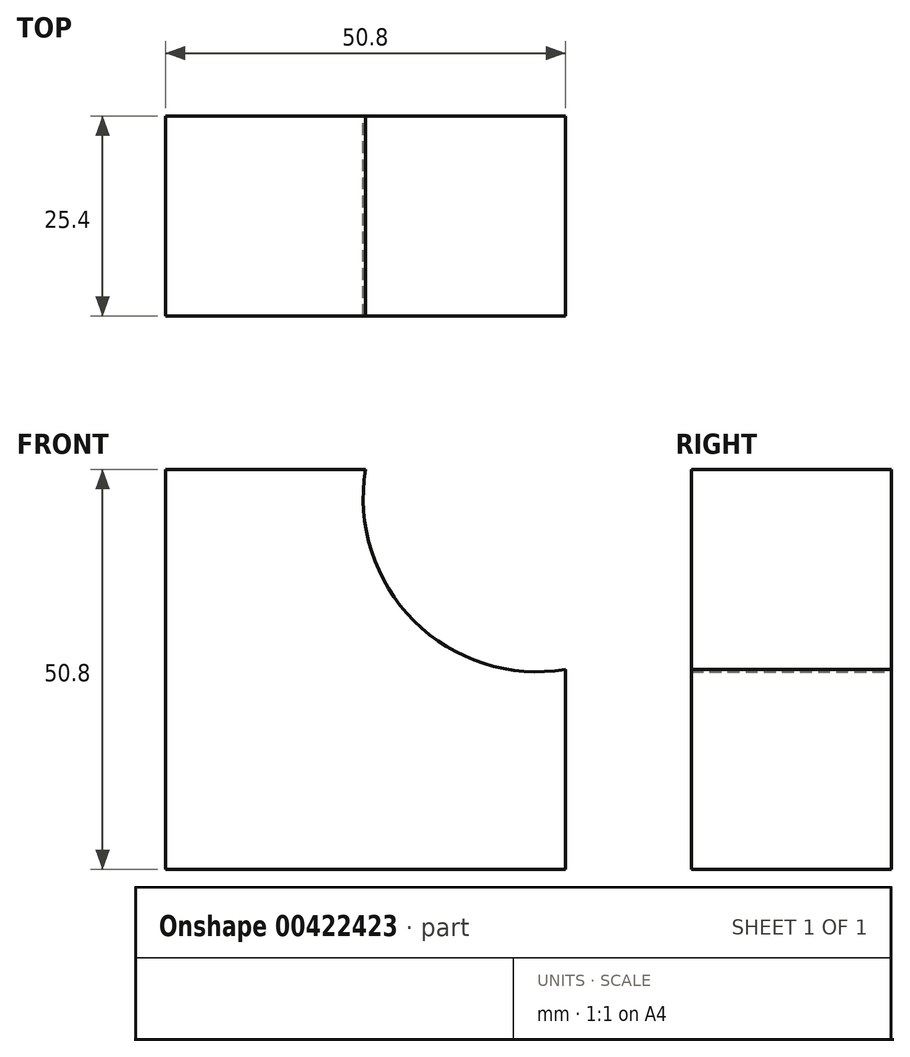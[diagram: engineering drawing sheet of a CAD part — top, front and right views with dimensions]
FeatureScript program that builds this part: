
annotation { "Feature Type Name" : "Feature", "Feature Type Description" : "" }
export const myFeature = defineFeature(function(context is Context, id is Id, definition is map)
    precondition{}
    {
        {
            var Q0;
            Q0=qCreatedBy(makeId("Front.planeOp"),FACE);
            var sketch = newSketch(context, id + "F0", { "sketchPlane" : qUnion([Q0])});
            skLineSegment(sketch, "E0", {"start": v(0, 0) * mm, "end": v(-50.8, 0) * mm});
            skLineSegment(sketch, "E1", {"start": v(-50.8, 0) * mm, "end": v(-50.8, 50.8) * mm});
            skLineSegment(sketch, "E2", {"start": v(-50.8, 50.8) * mm, "end": v(-25.4, 50.8) * mm});
            skLineSegment(sketch, "E3", {"start": v(0, 0) * mm, "end": v(0, 25.4) * mm});
            skArc(sketch, "E4", {"start": v(-25.4, 50.8) * mm, "mid": v(-19.24, 31.56) * mm, "end": v(0, 25.4) * mm});
            skSolve(sketch);
        }
        {
            var Q0;
            Q0 = qSketchRegion(id + "F0", true);
            extrude(context, id + "F1", {"entities" : qUnion([Q0]), "depth" : 25.4 * mm});
        }
    });
